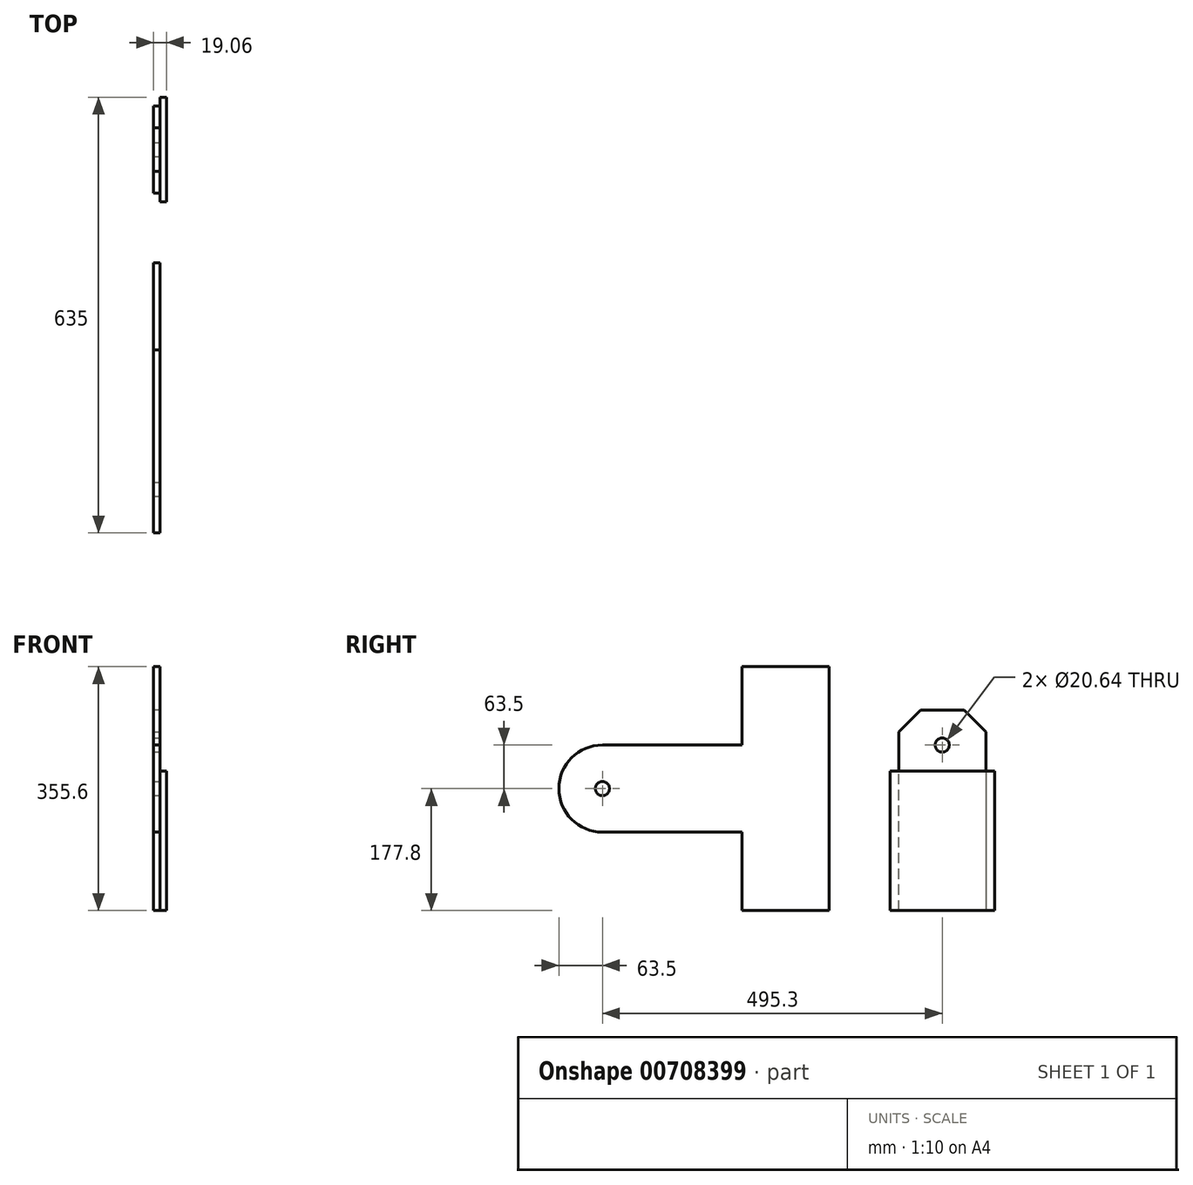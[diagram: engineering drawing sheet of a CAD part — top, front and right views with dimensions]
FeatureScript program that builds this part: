
annotation { "Feature Type Name" : "Feature", "Feature Type Description" : "" }
export const myFeature = defineFeature(function(context is Context, id is Id, definition is map)
    precondition{}
    {
        {
            var Q0;
            Q0=qCreatedBy(makeId("Right.planeOp"),FACE);
            var sketch = newSketch(context, id + "F0", { "sketchPlane" : qUnion([Q0])});
            skLineSegment(sketch, "E0", {"start": v(0, 0) * mm, "end": v(101.6, 0) * mm});
            skLineSegment(sketch, "E1", {"start": v(101.6, 0) * mm, "end": v(101.6, 292.1) * mm});
            skLineSegment(sketch, "E2", {"start": v(101.6, 292.1) * mm, "end": v(228.6, 292.1) * mm});
            skLineSegment(sketch, "E3", {"start": v(228.6, 292.1) * mm, "end": v(228.6, 0) * mm});
            skLineSegment(sketch, "E4", {"start": v(228.6, 0) * mm, "end": v(101.6, 0) * mm});
            skLineSegment(sketch, "E5", {"start": v(165.1, 0) * mm, "end": v(165.1, 241.3) * mm});
            skSolve(sketch);
        }
        {
            var Q0;
            {var subQ3=sQuery(id+"F0.wireOp",EDGE,"E1");Q0=makeQuery(id+"F0.imprint","IMPRINT",FACE,{"disambiguationData":[TD([[makeQuery(id+"F0.imprint","IMPRINT",EDGE,{"derivedFrom":subQ3}),-1.0]])]});}
            extrude(context, id + "F1", {"entities" : qUnion([Q0]), "oppositeDirection" : true, "depth" : 9.52 * mm, "offsetDistance" : 25.4 * mm});
        }
        {
            var Q0;
            Q0=makeQuery(id+"F1.opExtrude","SWEPT_EDGE",EDGE,{"disambiguationData":[OSD([sQuery(id+"F0.wireOp",EDGE,"E1"),sQuery(id+"F0.wireOp",EDGE,"E2")])]});
            var Q1;
            Q1=makeQuery(id+"F1.opExtrude","SWEPT_EDGE",EDGE,{"disambiguationData":[OSD([sQuery(id+"F0.wireOp",EDGE,"E2"),sQuery(id+"F0.wireOp",EDGE,"E3")])]});
            chamfer(context, id + "F2", {"entities" : qUnion([Q0, Q1]), "width" : 31.75 * mm, "tangentPropagation" : true});
        }
        {
            var Q0;
            Q0=sQuery(id+"F0.wireOp",VERTEX,"E5.end");
            var Q1;
            Q1=makeQuery(id+"F1.opExtrude","SWEPT_BODY",BODY,{"disambiguationData":[OSD([sQuery(id+"F0.wireOp",EDGE,"E1"),sQuery(id+"F0.wireOp",EDGE,"E2"),sQuery(id+"F0.wireOp",EDGE,"E3"),sQuery(id+"F0.wireOp",EDGE,"E4")])]});
            hole(context, id + "F3", {"style" : HoleStyle.SIMPLE, "endStyle" : HoleEndStyle.THROUGH, "holeDiameter" : 20.64 * mm, "majorDiameter" : 6.35 * mm, "isTappedThrough" : true, "tappedDepth" : 12.7 * mm, "tapClearance" : 3, "locations" : qUnion([Q0]), "scope" : qUnion([Q1])});
        }
        {
            var Q0;
            {var subQ3=sQuery(id+"F0.wireOp",EDGE,"E1");Q0=makeQuery(id+"F0.imprint","IMPRINT",FACE,{"disambiguationData":[TD([[makeQuery(id+"F0.imprint","IMPRINT",EDGE,{"derivedFrom":subQ3}),-1.0]])]});}
            var sketch = newSketch(context, id + "F4", { "sketchPlane" : qUnion([Q0])});
            skLineSegment(sketch, "E6", {"start": v(0, 0) * mm, "end": v(88.9, 0) * mm});
            skLineSegment(sketch, "E7", {"start": v(88.9, 0) * mm, "end": v(241.3, 0) * mm});
            skLineSegment(sketch, "E8", {"start": v(241.3, 0) * mm, "end": v(241.3, 203.2) * mm});
            skLineSegment(sketch, "E9", {"start": v(241.3, 203.2) * mm, "end": v(88.9, 203.2) * mm});
            skLineSegment(sketch, "E10", {"start": v(88.9, 203.2) * mm, "end": v(88.9, 0) * mm});
            skSolve(sketch);
        }
        {
            var Q0;
            {var subQ3=sQuery(id+"F4.wireOp",EDGE,"E10");Q0=makeQuery(id+"F4.imprint","IMPRINT",FACE,{"disambiguationData":[TD([[makeQuery(id+"F4.imprint","IMPRINT",EDGE,{"derivedFrom":subQ3}),1.0]])]});}
            var Q1;
            {var subQ0=sQuery(id+"F4.wireOp",EDGE,"E7");var subQ3=makeQuery(id+"F4.imprint","IMPRINT",VERTEX,{"derivedFrom":subQ0});Q1=makeQuery(id+"F4.imprint","IMPRINT",FACE,{"disambiguationData":[TD([[makeQuery(id+"F4.imprint","IMPRINT",EDGE,{"disambiguationData":[TD([[subQ3,1.0]])],"derivedFrom":subQ0}),-1.0]])]});}
            var Q2;
            {var subQ3=sQuery(id+"F4.wireOp",EDGE,"E8");Q2=makeQuery(id+"F4.imprint","IMPRINT",FACE,{"disambiguationData":[TD([[makeQuery(id+"F4.imprint","IMPRINT",EDGE,{"derivedFrom":subQ3}),1.0]])]});}
            extrude(context, id + "F5", {"entities" : qUnion([Q0, Q1, Q2]), "operationType" : NewBodyOperationType.ADD, "depth" : 9.52 * mm, "offsetDistance" : 25.4 * mm});
        }
        {
            var Q0;
            Q0=qCreatedBy(makeId("Right.planeOp"),FACE);
            var sketch = newSketch(context, id + "F6", { "sketchPlane" : qUnion([Q0])});
            skLineSegment(sketch, "E11", {"start": v(0, 0) * mm, "end": v(0, 355.6) * mm});
            skLineSegment(sketch, "E12", {"start": v(0, 355.6) * mm, "end": v(-127, 355.6) * mm});
            skLineSegment(sketch, "E13", {"start": v(0, 0) * mm, "end": v(-127, 0) * mm});
            skLineSegment(sketch, "E14", {"start": v(-127, 0) * mm, "end": v(-127, 114.3) * mm});
            skLineSegment(sketch, "E15", {"start": v(-127, 355.6) * mm, "end": v(-127, 241.3) * mm});
            skLineSegment(sketch, "E16", {"start": v(-127, 241.3) * mm, "end": v(-330.2, 241.3) * mm});
            skLineSegment(sketch, "E17", {"start": v(-127, 114.3) * mm, "end": v(-330.2, 114.3) * mm});
            skArc(sketch, "E18", {"start": v(-330.2, 241.3) * mm, "mid": v(-393.7, 177.8) * mm, "end": v(-330.2, 114.3) * mm});
            skSolve(sketch);
        }
        {
            var Q0;
            Q0=makeQuery(id+"F6.imprint","IMPRINT",FACE,{"disambiguationData":[TD([[makeQuery(id+"F6.imprint","IMPRINT",EDGE,{"derivedFrom":sQuery(id+"F6.wireOp",EDGE,"E11")}),1.0]])]});
            extrude(context, id + "F7", {"entities" : qUnion([Q0]), "oppositeDirection" : true, "depth" : 9.52 * mm, "offsetDistance" : 25.4 * mm});
        }
        {
            var Q0;
            Q0=sQuery(id+"F6.wireOp",VERTEX,"E18.center");
            var Q1;
            Q1=makeQuery(id+"F7.opExtrude","SWEPT_BODY",BODY,{"disambiguationData":[OSD([sQuery(id+"F6.wireOp",EDGE,"E11"),sQuery(id+"F6.wireOp",EDGE,"E12"),sQuery(id+"F6.wireOp",EDGE,"E13"),sQuery(id+"F6.wireOp",EDGE,"E14"),sQuery(id+"F6.wireOp",EDGE,"E15"),sQuery(id+"F6.wireOp",EDGE,"E16"),sQuery(id+"F6.wireOp",EDGE,"E17"),sQuery(id+"F6.wireOp",EDGE,"E18")])]});
            hole(context, id + "F8", {"style" : HoleStyle.SIMPLE, "endStyle" : HoleEndStyle.THROUGH, "holeDiameter" : 20.64 * mm, "majorDiameter" : 6.35 * mm, "isTappedThrough" : true, "tappedDepth" : 12.7 * mm, "tapClearance" : 3, "locations" : qUnion([Q0]), "scope" : qUnion([Q1])});
        }
    });
